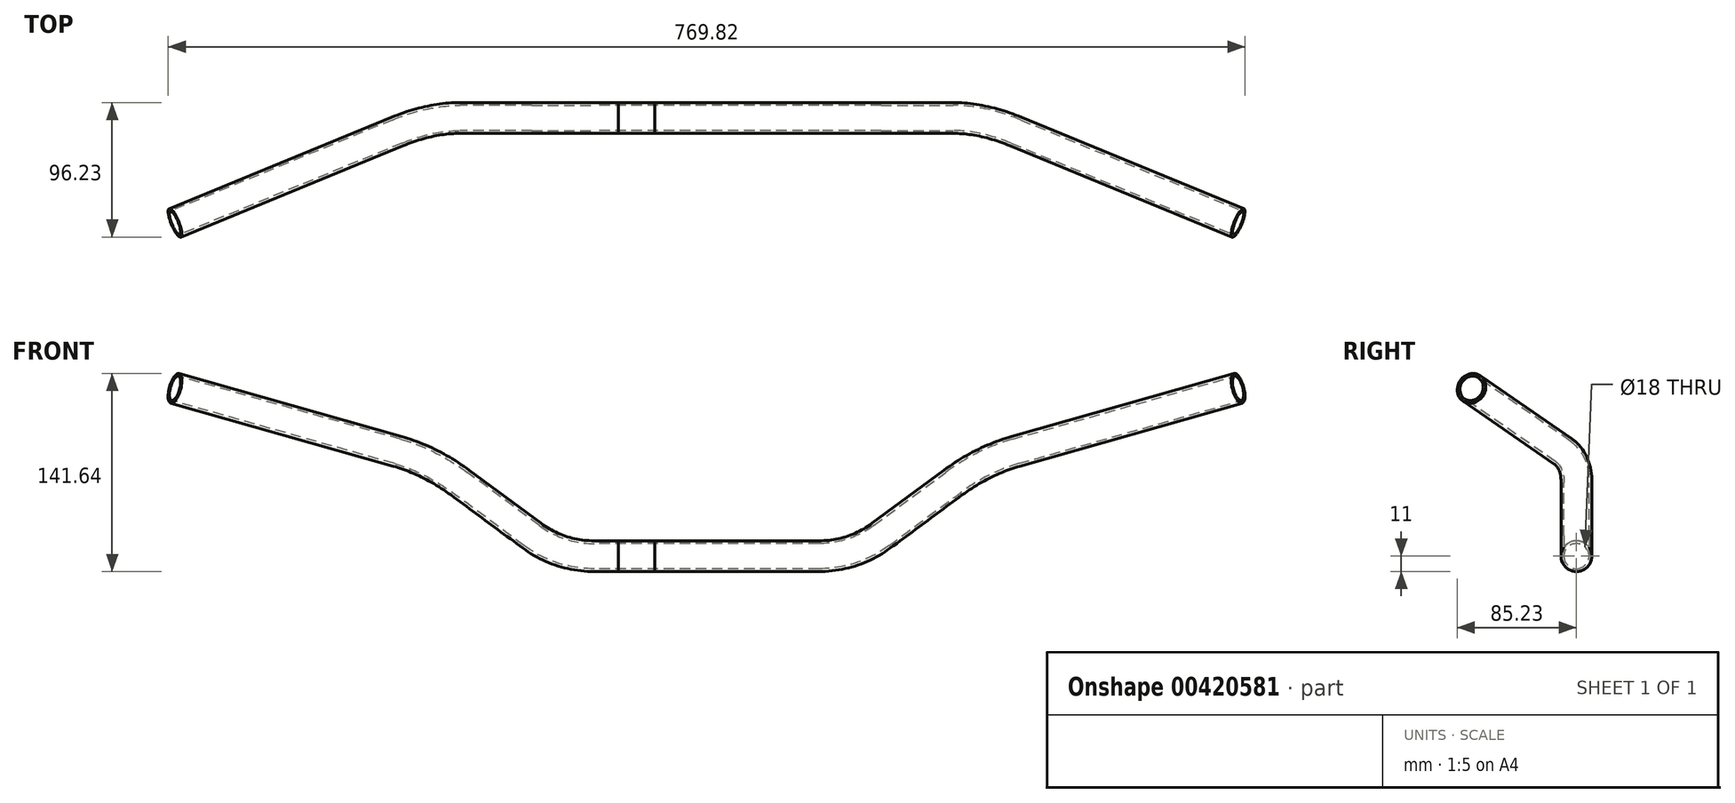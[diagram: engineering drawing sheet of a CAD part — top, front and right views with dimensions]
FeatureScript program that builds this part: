
annotation { "Feature Type Name" : "Feature", "Feature Type Description" : "" }
export const myFeature = defineFeature(function(context is Context, id is Id, definition is map)
    precondition{}
    {
        {
            var Q0;
            Q0=qCreatedBy(makeId("Front.planeOp"),FACE);
            var sketch = newSketch(context, id + "F0", { "sketchPlane" : qUnion([Q0])});
            skLineSegment(sketch, "E0", {"start": v(-80.3, 0) * mm, "end": v(0, 0) * mm});
            skArc(sketch, "E1", {"start": v(-124.86, 14.67) * mm, "mid": v(-103.76, 3.76) * mm, "end": v(-80.3, 0) * mm});
            skLineSegment(sketch, "E2", {"start": v(-124.86, 14.67) * mm, "end": v(-197.5, 68.33) * mm});
            skLineSegment(sketch, "E3", {"start": v(-80.3, 0) * mm, "end": v(-173.53, 0) * mm, "construction": true});
            skLineSegment(sketch, "E4", {"start": v(-197.5, 68.33) * mm, "end": v(-105, 0) * mm, "construction": true});
            skSolve(sketch);
        }
        {
            var Q0;
            Q0=qCreatedBy(makeId("Right.planeOp"),FACE);
            var sketch = newSketch(context, id + "F1", { "sketchPlane" : qUnion([Q0])});
            skCircle(sketch, "E5", {"center": v(0, 0) * mm, "radius": 11 * mm});
            skCircle(sketch, "E6", {"center": v(0, 0) * mm, "radius": 9 * mm});
            skSolve(sketch);
        }
        {
            var Q0;
            Q0=qCreatedBy(makeId("Front.planeOp"),FACE);
            cPlane(context, id + "F2", {"entities" : qUnion([Q0]), "cplaneType" : CPlaneType.OFFSET, "offset" : 75 * mm, "width" : 150 * mm, "height" : 150 * mm});
        }
        {
            var Q0;
            Q0=qCreatedBy(id+"F2.planeOp",FACE);
            var sketch = newSketch(context, id + "F3", { "sketchPlane" : qUnion([Q0])});
            skPoint(sketch, "E7", {"position": v(-380, 120) * mm});
            skLineSegment(sketch, "E8", {"start": v(-380, 120) * mm, "end": v(-380, 0) * mm});
            skSolve(sketch);
        }
        {
            var Q0;
            Q0=sQuery(id+"F3.wireOp",VERTEX,"E7");
            var Q1;
            Q1=sQuery(id+"F3.wireOp",VERTEX,"E8.end");
            var Q2;
            Q2=sQuery(id+"F0.wireOp",VERTEX,"E4.start");
            cPlane(context, id + "F4", {"entities" : qUnion([Q0, Q1, Q2]), "cplaneType" : CPlaneType.THREE_POINT, "offset" : 25 * mm, "width" : 150 * mm, "height" : 150 * mm});
        }
        {
            var Q0;
            Q0=qCreatedBy(id+"F4.planeOp",FACE);
            var sketch = newSketch(context, id + "F5", { "sketchPlane" : qUnion([Q0])});
            skLineSegment(sketch, "E9", {"start": v(379.99, 120) * mm, "end": v(182.68, 68.33) * mm, "construction": true});
            skSolve(sketch);
        }
        {
            var Q0;
            Q0=sQuery(id+"F0.wireOp",VERTEX,"E2.start");
            var Q1;
            Q1=sQuery(id+"F3.wireOp",VERTEX,"E7");
            var Q2;
            Q2=sQuery(id+"F5.wireOp",VERTEX,"E9.end");
            cPlane(context, id + "F6", {"entities" : qUnion([Q0, Q1, Q2]), "cplaneType" : CPlaneType.THREE_POINT, "offset" : 25 * mm, "width" : 150 * mm, "height" : 150 * mm});
        }
        {
            var Q0;
            Q0=qCreatedBy(id+"F6.planeOp",FACE);
            var sketch = newSketch(context, id + "F7", { "sketchPlane" : qUnion([Q0])});
            skLineSegment(sketch, "E10", {"start": v(-400.93, 38.86) * mm, "end": v(-223.61, 49.2) * mm});
            skLineSegment(sketch, "E11", {"start": v(-173.67, 39.11) * mm, "end": v(-116.27, 10.9) * mm});
            skArc(sketch, "E12", {"start": v(-173.67, 39.11) * mm, "mid": v(-197.99, 47.4) * mm, "end": v(-223.61, 49.2) * mm});
            skSolve(sketch);
        }
        {
            var Q0;
            Q0=makeQuery(id+"F1.imprint","IMPRINT",FACE,{"disambiguationData":[TD([[makeQuery(id+"F1.imprint","IMPRINT",EDGE,{"derivedFrom":sQuery(id+"F1.wireOp",EDGE,"E5")}),1.0]])]});
            var Q1;
            Q1=sQuery(id+"F0.wireOp",EDGE,"E0");
            var Q2;
            Q2=sQuery(id+"F0.wireOp",EDGE,"E1");
            var Q3;
            Q3=sQuery(id+"F7.wireOp",EDGE,"E11");
            var Q4;
            Q4=sQuery(id+"F7.wireOp",EDGE,"E12");
            var Q5;
            Q5=sQuery(id+"F7.wireOp",EDGE,"E10");
            sweep(context, id + "F8", {"profiles" : qUnion([Q0]), "path" : qUnion([Q1, Q2, Q3, Q4, Q5])});
        }
        {
            var Q0;
            Q0=makeQuery(id+"F8.opSweep","SWEPT_BODY",BODY,{"disambiguationData":[OSD([sQuery(id+"F1.wireOp",EDGE,"E5"),sQuery(id+"F1.wireOp",EDGE,"E6"),sQuery(id+"F7.wireOp",EDGE,"E10")])]});
            var Q1;
            Q1=makeQuery(id+"F1.imprint","IMPRINT",FACE,{"disambiguationData":[TD([[makeQuery(id+"F1.imprint","IMPRINT",EDGE,{"derivedFrom":sQuery(id+"F1.wireOp",EDGE,"E5")}),1.0]])]});
            mirror(context, id + "F9", {"operationType" : NewBodyOperationType.ADD, "entities" : qUnion([Q0]), "mirrorPlane" : qUnion([Q1])});
        }
        {
            var Q0;
            Q0=qCreatedBy(makeId("Front.planeOp"),FACE);
            var sketch = newSketch(context, id + "F10", { "sketchPlane" : qUnion([Q0])});
            skLineSegment(sketch, "E13.bottom", {"start": v(-63, 12.9) * mm, "end": v(-37, 12.9) * mm});
            skLineSegment(sketch, "E13.top", {"start": v(-63, 10.9) * mm, "end": v(-37, 10.9) * mm});
            skLineSegment(sketch, "E13.left", {"start": v(-63, 12.9) * mm, "end": v(-63, 10.9) * mm});
            skLineSegment(sketch, "E13.right", {"start": v(-37, 12.9) * mm, "end": v(-37, 10.9) * mm});
            skLineSegment(sketch, "E14", {"start": v(-50, 12.9) * mm, "end": v(-50, 10.9) * mm, "construction": true});
            skLineSegment(sketch, "E15", {"start": v(0, 0) * mm, "end": v(-74.04, 0) * mm, "construction": true});
            skSolve(sketch);
        }
        {
            var Q0;
            Q0 = qSketchRegion(id + "F10", true);
            var Q1;
            Q1=sQuery(id+"F10.wireOp",EDGE,"E15");
            revolve(context, id + "F11", {"operationType" : NewBodyOperationType.REMOVE, "entities" : qUnion([Q0]), "axis" : qUnion([Q1]), "revolveType" : RevolveType.FULL, "oppositeDirection" : true});
        }
    });
